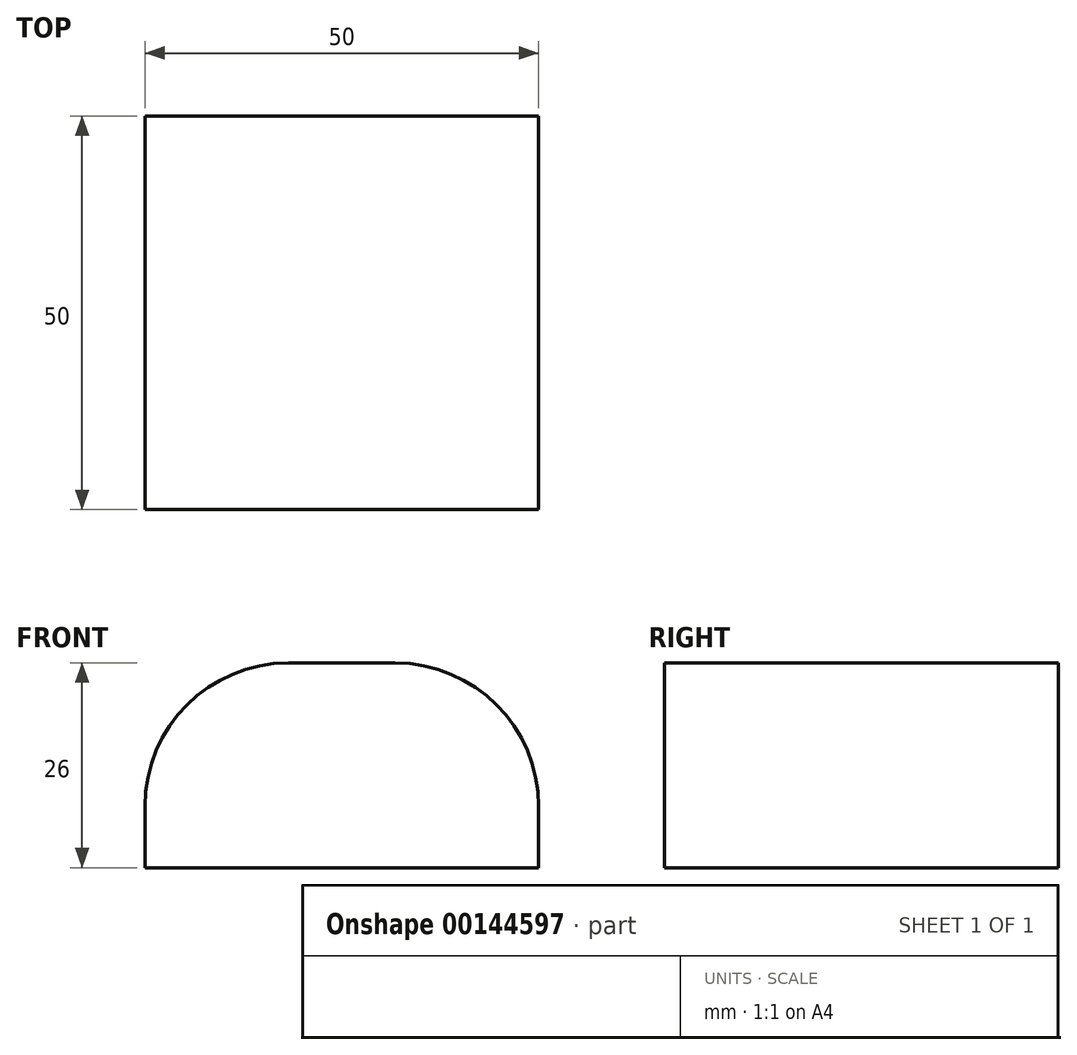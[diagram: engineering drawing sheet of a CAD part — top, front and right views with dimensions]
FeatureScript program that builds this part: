
annotation { "Feature Type Name" : "Feature", "Feature Type Description" : "" }
export const myFeature = defineFeature(function(context is Context, id is Id, definition is map)
    precondition{}
    {
        {
            var Q0;
            Q0=qCreatedBy(makeId("Top.planeOp"),FACE);
            var sketch = newSketch(context, id + "F0", { "sketchPlane" : qUnion([Q0])});
            skLineSegment(sketch, "E0.bottom", {"start": v(25, 25) * mm, "end": v(-25, 25) * mm});
            skLineSegment(sketch, "E0.top", {"start": v(25, -25) * mm, "end": v(-25, -25) * mm});
            skLineSegment(sketch, "E0.left", {"start": v(25, 25) * mm, "end": v(25, -25) * mm});
            skLineSegment(sketch, "E0.right", {"start": v(-25, 25) * mm, "end": v(-25, -25) * mm});
            skPoint(sketch, "E0.middle", {"position": v(0, 0) * mm});
            skSolve(sketch);
        }
        {
            var Q0;
            Q0 = qSketchRegion(id + "F0", true);
            extrude(context, id + "F1", {"entities" : qUnion([Q0]), "depth" : 26 * mm});
        }
        {
            var Q0;
            Q0=makeQuery(id+"F1.opExtrude","SWEPT_FACE",FACE,{"disambiguationData":[OSD([sQuery(id+"F0.wireOp",EDGE,"E0.top")])]});
            var sketch = newSketch(context, id + "F2", { "sketchPlane" : qUnion([Q0])});
            skArc(sketch, "E1", {"start": v(25, 7.8) * mm, "mid": v(19.67, 20.67) * mm, "end": v(6.8, 26) * mm});
            skLineSegment(sketch, "E2", {"start": v(0, 0) * mm, "end": v(0, 52.95) * mm, "construction": true});
            skPoint(sketch, "E2.endSnap0", {"position": v(0, 26) * mm});
            skLineSegment(sketch, "E3", {"start": v(25, 7.8) * mm, "end": v(25, 26) * mm});
            skLineSegment(sketch, "E4", {"start": v(25, 26) * mm, "end": v(6.8, 26) * mm});
            skLineSegment(sketch, "E5.MirrorCS", {"start": v(-25, 7.8) * mm, "end": v(-25, 26) * mm});
            skLineSegment(sketch, "E6.MirrorCS", {"start": v(-25, 26) * mm, "end": v(-6.8, 26) * mm});
            skArc(sketch, "E7.MirrorCS", {"start": v(-25, 7.8) * mm, "mid": v(-19.67, 20.67) * mm, "end": v(-6.8, 26) * mm});
            skSolve(sketch);
        }
        {
            var Q0;
            Q0 = qSketchRegion(id + "F2", true);
            extrude(context, id + "F3", {"entities" : qUnion([Q0]), "operationType" : NewBodyOperationType.REMOVE, "endBound" : BoundingType.THROUGH_ALL, "oppositeDirection" : true, "depth" : 25 * mm});
        }
    });
